# Revit family: Adaptador 4 MTP
name_source: partatom
category: Installations électriques
units: mm (PartAtom-declared; Revit-internal decimal feet)

## family parameters
Basée sur le plan de construction = Non
Conserver l'orientation des annotations = Non
Cote de connecteur circulaire = Utiliser le diamètre
Couper avec des vides une fois chargée = Non
Partagée = Non
Point de calcul de pièce = Non
Toujours verticalement = Oui
Type d'élément = Normal

## types (2) — shared parameters
Altura = 23 mm  [stored 0.0754593 ft]
Altura de la apertura = 6.5 mm
Altura de los conectores = 10 mm  [stored 0.0328084 ft]
Anchura (mm) = 108.8 mm
Anchura de la apertura = 8.35 mm  [stored 0.027395 ft]
Anchura de los conectores = 13.5 mm  [stored 0.0442913 ft]
Clasificación ETIM = EC001130
Color = IDS_NOIR
E-catalogo enlace = https://www.legrand.fr
Función = Paneles de interconexión con optical conector Legrand
IK = IK04
IP = IP20
Numero RAL = 9017
Número de conectores = 4
Profundidad = 44.7 mm
Temperatura de almacenamiento = -10°C à 60°C
Temperatura operativa = -10°C à 60°C
Tipo de conector externo = MT_MPO
Tipo de conector interno = MT_MPO
zero-valued in all types: Elévation par défaut

## per-type parameters (varying)
| type | Color de los conectores | EAN | Número de pieza Legrand | Tipo de la fibra óptica |
| Adaptador 4 MTP monomodal | IDS_VERT | 3414970962041 | 032133 | unimodal |
| Adaptador 4 MTP multimodal | IDS_JAUNE | 3414970962065 | 032134 | Mutlimodal |

note: column(s) folded — value = type name in every type: Formulación BIM

note: [stored X ft] marks values corroborated as IEEE doubles in the binary element streams (Revit-internal decimal feet)
